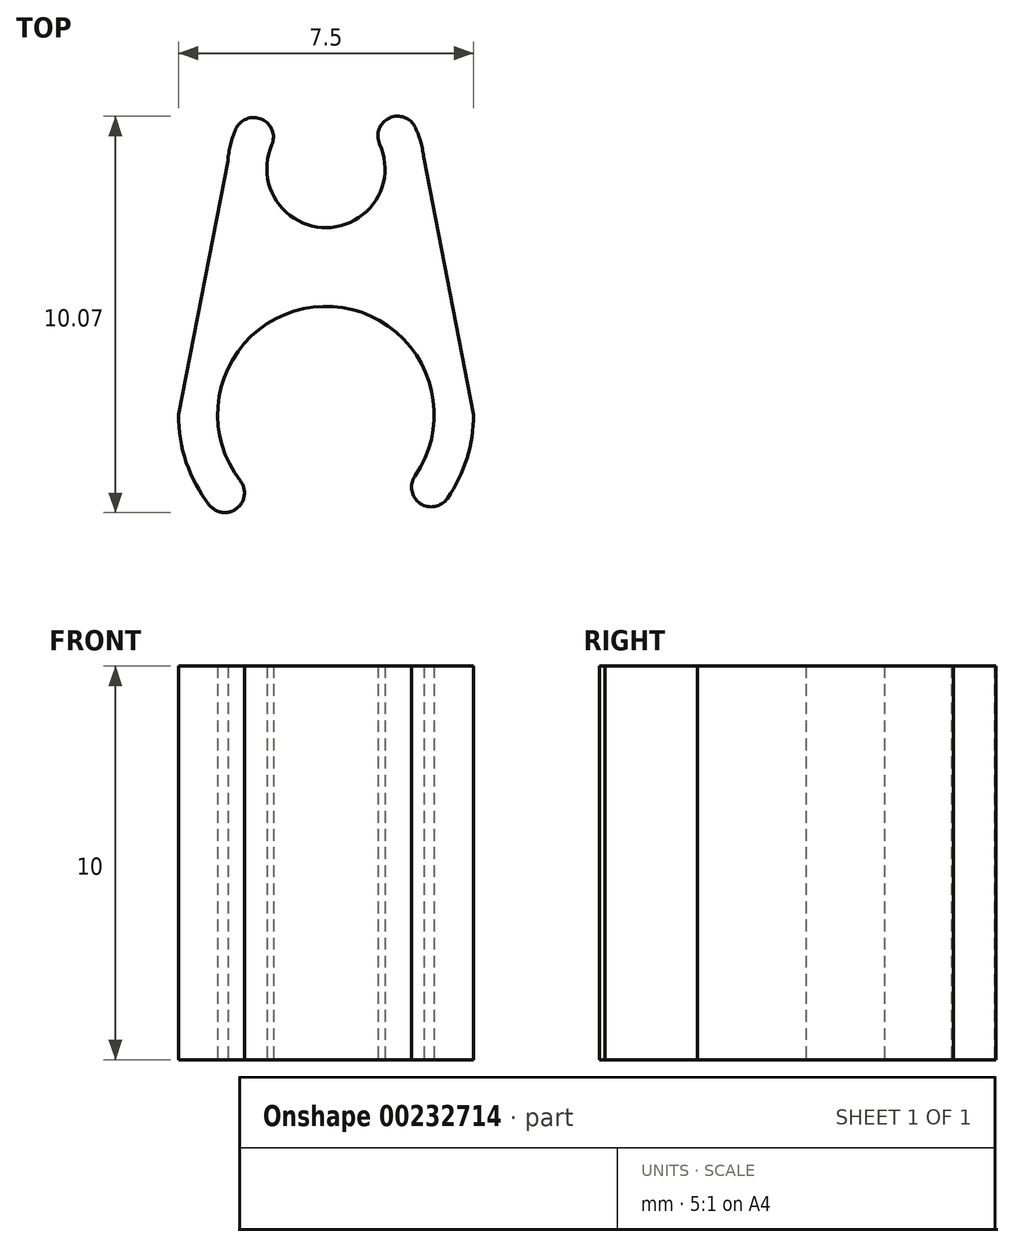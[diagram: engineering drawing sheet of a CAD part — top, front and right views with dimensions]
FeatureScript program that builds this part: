
annotation { "Feature Type Name" : "Feature", "Feature Type Description" : "" }
export const myFeature = defineFeature(function(context is Context, id is Id, definition is map)
    precondition{}
    {
        {
            var Q0;
            Q0=qCreatedBy(makeId("Top.planeOp"),FACE);
            var sketch = newSketch(context, id + "F0", { "sketchPlane" : qUnion([Q0])});
            skCircle(sketch, "E0", {"center": v(0, 0) * mm, "radius": 3.75 * mm});
            skCircle(sketch, "E1", {"center": v(0, 0) * mm, "radius": 2.75 * mm});
            skLineSegment(sketch, "E2", {"start": v(-3.75, 0) * mm, "end": v(-3.75, 7.01) * mm});
            skLineSegment(sketch, "E3", {"start": v(3.75, 0) * mm, "end": v(3.75, -10.8) * mm});
            skCircle(sketch, "E4", {"center": v(0, 6.25) * mm, "radius": 1.5 * mm});
            skCircle(sketch, "E5", {"center": v(0, 6.25) * mm, "radius": 2.5 * mm});
            skLineSegment(sketch, "E6", {"start": v(-2.5, 6.45) * mm, "end": v(-3.75, 0) * mm});
            skLineSegment(sketch, "E7", {"start": v(3.75, 0) * mm, "end": v(2.49, 6.5) * mm});
            skLineSegment(sketch, "E8", {"start": v(0, 0) * mm, "end": v(-2.58, -2.72) * mm});
            skLineSegment(sketch, "E9", {"start": v(0, 0) * mm, "end": v(2.72, -2.58) * mm});
            skLineSegment(sketch, "E10", {"start": v(0, 6.25) * mm, "end": v(-1.97, 7.79) * mm});
            skLineSegment(sketch, "E11", {"start": v(0, 6.25) * mm, "end": v(1.94, 7.82) * mm});
            skSolve(sketch);
        }
        {
            var Q0;
            {var subQ3=sQuery(id+"F0.wireOp",EDGE,"E10");var subQ5=sQuery(id+"F0.wireOp",EDGE,"E4");var subQ6=makeQuery(id+"F0.imprint","INTERSECT",VERTEX,{"derivedFrom":[subQ5,subQ3]});Q0=makeQuery(id+"F0.imprint","IMPRINT",FACE,{"disambiguationData":[TD([[makeQuery(id+"F0.imprint","IMPRINT",EDGE,{"disambiguationData":[TD([[subQ6,-1.0]])],"derivedFrom":subQ5}),-1.0]])]});}
            var Q1;
            {var subQ0=sQuery(id+"F0.wireOp",EDGE,"E7");var subQ1=sQuery(id+"F0.wireOp",EDGE,"E0");var subQ13=makeQuery(id+"F0.imprint","INTERSECT",VERTEX,{"disambiguationData":[OD(1.0)],"derivedFrom":[subQ1,subQ0]});Q1=makeQuery(id+"F0.imprint","IMPRINT",FACE,{"disambiguationData":[TD([[makeQuery(id+"F0.imprint","IMPRINT",EDGE,{"disambiguationData":[TD([[subQ13,-1.0]])],"derivedFrom":subQ1}),1.0]])]});}
            var Q2;
            {var subQ0=sQuery(id+"F0.wireOp",EDGE,"E6");var subQ1=sQuery(id+"F0.wireOp",EDGE,"E0");var subQ2=makeQuery(id+"F0.imprint","INTERSECT",VERTEX,{"disambiguationData":[OD(1.0)],"derivedFrom":[subQ1,subQ0]});Q2=makeQuery(id+"F0.imprint","IMPRINT",FACE,{"disambiguationData":[TD([[makeQuery(id+"F0.imprint","IMPRINT",EDGE,{"disambiguationData":[TD([[subQ2,1.0]])],"derivedFrom":subQ1}),-1.0]])]});}
            var Q3;
            {var subQ0=sQuery(id+"F0.wireOp",EDGE,"E7");var subQ1=sQuery(id+"F0.wireOp",EDGE,"E0");var subQ2=makeQuery(id+"F0.imprint","INTERSECT",VERTEX,{"disambiguationData":[OD(1.0)],"derivedFrom":[subQ1,subQ0]});Q3=makeQuery(id+"F0.imprint","IMPRINT",FACE,{"disambiguationData":[TD([[makeQuery(id+"F0.imprint","IMPRINT",EDGE,{"disambiguationData":[TD([[subQ2,-1.0]])],"derivedFrom":subQ1}),-1.0]])]});}
            extrude(context, id + "F1", {"entities" : qUnion([Q0, Q1, Q2, Q3]), "depth" : 10 * mm});
        }
        {
            var Q0;
            Q0=makeQuery(id+"F1.opExtrude","SWEPT_EDGE",EDGE,{"disambiguationData":[OSD([sQuery(id+"F0.wireOp",EDGE,"E4"),sQuery(id+"F0.wireOp",EDGE,"E10")])]});
            var Q1;
            Q1=makeQuery(id+"F1.opExtrude","SWEPT_EDGE",EDGE,{"disambiguationData":[OSD([sQuery(id+"F0.wireOp",EDGE,"E4"),sQuery(id+"F0.wireOp",EDGE,"E11")])]});
            var Q2;
            Q2=makeQuery(id+"F1.opExtrude","SWEPT_EDGE",EDGE,{"disambiguationData":[OSD([sQuery(id+"F0.wireOp",EDGE,"E1"),sQuery(id+"F0.wireOp",EDGE,"E8")])]});
            var Q3;
            Q3=makeQuery(id+"F1.opExtrude","SWEPT_EDGE",EDGE,{"disambiguationData":[OSD([sQuery(id+"F0.wireOp",EDGE,"E1"),sQuery(id+"F0.wireOp",EDGE,"E9")])]});
            var Q4;
            Q4=makeQuery(id+"F1.opExtrude","SWEPT_EDGE",EDGE,{"disambiguationData":[OSD([sQuery(id+"F0.wireOp",EDGE,"E5"),sQuery(id+"F0.wireOp",EDGE,"E10")])]});
            var Q5;
            Q5=makeQuery(id+"F1.opExtrude","SWEPT_EDGE",EDGE,{"disambiguationData":[OSD([sQuery(id+"F0.wireOp",EDGE,"E5"),sQuery(id+"F0.wireOp",EDGE,"E11")])]});
            var Q6;
            Q6=makeQuery(id+"F1.opExtrude","SWEPT_EDGE",EDGE,{"disambiguationData":[OSD([sQuery(id+"F0.wireOp",EDGE,"E0"),sQuery(id+"F0.wireOp",EDGE,"E9")])]});
            var Q7;
            Q7=makeQuery(id+"F1.opExtrude","SWEPT_EDGE",EDGE,{"disambiguationData":[OSD([sQuery(id+"F0.wireOp",EDGE,"E0"),sQuery(id+"F0.wireOp",EDGE,"E8")])]});
            fillet(context, id + "F2", {"entities" : qUnion([Q0, Q1, Q2, Q3, Q4, Q5, Q6, Q7]), "radius" : 0.5 * mm, "tangentPropagation" : true, "allowEdgeOverflow" : false});
        }
    });
